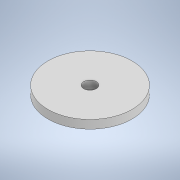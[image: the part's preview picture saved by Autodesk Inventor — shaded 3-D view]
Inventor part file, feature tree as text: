
AUTODESK INVENTOR PART (.ipt)
format: ipt  version: 2022 (Build 260153000, 153)  size: 95,232 bytes
history: native  units: mm
features: extrude x1, sketch x1
ambient origin geometry x8: Origin, YZ Plane, XZ Plane, XY Plane, X Axis, Y Axis, Z Axis, Center Point
bodies: Solid1 (feature_tree)
feature tree (2):
  extrude  "Extrusion1"  Depth=2.0mm
  sketch  "Sketch1"  dims[d0=20.0mm d1=3.0mm d2=2.0mm d3=0.0mm]
